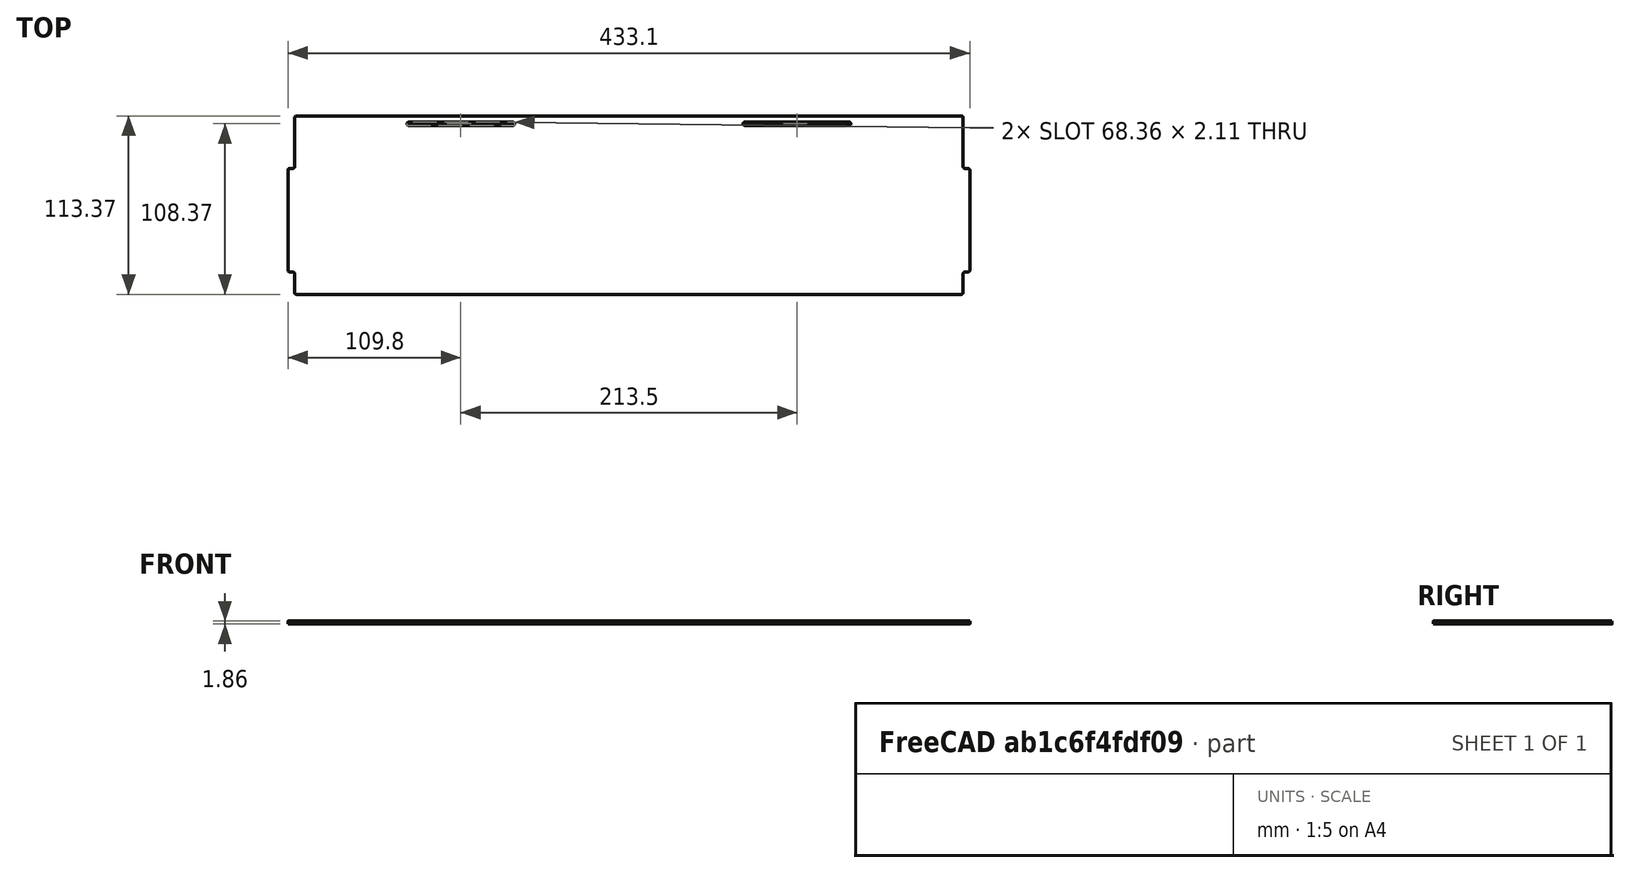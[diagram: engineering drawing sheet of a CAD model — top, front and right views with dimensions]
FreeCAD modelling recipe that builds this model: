
FCSTD DOCUMENT  (FreeCAD 1.0R38641 +468 (Git))
Label: panel_top_and_bottom
License: All rights reserved
LicenseURL: https://en.wikipedia.org/wiki/All_rights_reserved
objects: PartDesign::SubShapeBinder×2, Sketcher::SketchObject×1, PartDesign::Pad×1, PartDesign::Body×1
note: 8 computed .brp shape members not serialized (recipe doc carries the construction recipe); baked Part::Feature solids carry a one-line shape summary decoded from their .brp
EXTERNAL_REF file=dimensions.FCStd obj=VarSet
EXTERNAL_REF file=panel_side.FCStd obj=Sketch
EXTERNAL_REF file=panel_side.FCStd obj=Body001
EXTERNAL_REF file=../third_party/tiptop_z_rail.FCStd obj=Body

FEATURE [PartDesign::SubShapeBinder] Binder  label="SidePanelBinder"
  BindCopyOnChange = 0
  BindMode = 0
  ClaimChildren = false
  Context = -> Body [Binder.]
  Fuse = false
  MakeFace = true
  OffsetFill = false
  OffsetIntersection = false
  OffsetJoinType = 0
  OffsetOpenResult = false
  PartialLoad = false
  Refine = true
  Relative = true
  Support = -> [<external panel_side.FCStd>#Body001]
  _Version = 2
FEATURE [PartDesign::SubShapeBinder] Binder001  label="RailBinder"
  BindCopyOnChange = 0
  BindMode = 0
  ClaimChildren = false
  Context = -> Body [Binder001.]
  Fuse = false
  MakeFace = true
  OffsetFill = false
  OffsetIntersection = false
  OffsetJoinType = 0
  OffsetOpenResult = false
  PartialLoad = false
  Refine = true
  Relative = true
  Support = -> [<external ../third_party/tiptop_z_rail.FCStd>#Body]
  _Version = 2
FEATURE [Sketcher::SketchObject] Sketch
  ArcFitTolerance = 1e-06
  AttachmentOffset = pos=(0,0,0.127) rot=(0,0,1;0rad)
  AttachmentSupport = -> [Binder,Binder001]
  ExternalGeometry = -> [Binder,Binder001]
  FullyConstrained = true
  MakeInternals = false
  MapMode = 5
  Placement = pos=(0,1.3e-15,4.0729) rot=(0,0,1;0rad)
  expr: .AttachmentOffset.Base.z = dimensions#VarSet.EnclosureFinishThickness
  expr: Constraints[102] = dimensions#VarSet.EnclosureFinishThickness
  expr: Constraints[27] = 2 * <<dimensions>>#VarSet.EnclosureFinishThickness
  expr: Constraints[78] = <<dimensions>>#VarSet.EnclosureTotalThickness + 2 * <<dimensions>>#VarSet.EnclosureFinishThickness
  expr: Constraints[87] = <<dimensions>>#VarSet.EnclosureCornerRadius
  expr: Constraints[89] = panel_side#<<Sketch>>.Constraints.EdgeToSlot
  expr: Constraints[90] = panel_side#<<Sketch>>.Constraints.SlotLength
  sketch-geometry (44):
    g0: LineSegment StartX=-3.0542 StartY=96.721 StartZ=0 EndX=-3.0542 EndY=33.379 EndZ=0
    g1: LineSegment StartX=430.054 StartY=33.379 StartZ=0 EndX=430.054 EndY=96.721 EndZ=0
    g2: ArcOfCircle CenterX=-1.8542 CenterY=96.721 CenterZ=0 NormalX=0 NormalY=0 NormalZ=1 AngleXU=0 Radius=1.2 StartAngle=1.5708 EndAngle=3.14159
    g3: ArcOfCircle CenterX=-1.8542 CenterY=33.379 CenterZ=0 NormalX=0 NormalY=0 NormalZ=1 AngleXU=0 Radius=1.2 StartAngle=3.14159 EndAngle=4.71239
    g4: ArcOfCircle CenterX=428.854 CenterY=33.379 CenterZ=0 NormalX=0 NormalY=0 NormalZ=1 AngleXU=0 Radius=1.2 StartAngle=4.71239 EndAngle=6.28319
    g5: ArcOfCircle CenterX=428.854 CenterY=96.721 CenterZ=0 NormalX=0 NormalY=0 NormalZ=1 AngleXU=0 Radius=1.2 StartAngle=-4.4e-15 EndAngle=1.5708
    g6: LineSegment StartX=2.4 StartY=17.927 StartZ=0 EndX=424.6 EndY=17.927 EndZ=0
    g7: LineSegment StartX=424.6 StartY=131.3 StartZ=0 EndX=2.4 EndY=131.3 EndZ=0
    g8: ArcOfCircle CenterX=2.4 CenterY=130.1 CenterZ=0 NormalX=0 NormalY=0 NormalZ=1 AngleXU=0 Radius=1.2 StartAngle=1.5708 EndAngle=3.14159
    g9: ArcOfCircle CenterX=2.4 CenterY=19.127 CenterZ=0 NormalX=0 NormalY=0 NormalZ=1 AngleXU=0 Radius=1.2 StartAngle=3.14159 EndAngle=4.71239
    g10: ArcOfCircle CenterX=424.6 CenterY=19.127 CenterZ=0 NormalX=0 NormalY=0 NormalZ=1 AngleXU=0 Radius=1.2 StartAngle=4.71239 EndAngle=6.28319
    g11: ArcOfCircle CenterX=424.6 CenterY=130.1 CenterZ=0 NormalX=0 NormalY=0 NormalZ=1 AngleXU=0 Radius=1.2 StartAngle=-2.7e-15 EndAngle=1.5708
    g12: LineSegment StartX=428.854 StartY=97.921 StartZ=0 EndX=427 EndY=97.921 EndZ=0
    g13: LineSegment StartX=425.8 StartY=99.121 StartZ=0 EndX=425.8 EndY=130.1 EndZ=0
    g14: LineSegment StartX=425.8 StartY=19.127 StartZ=0 EndX=425.8 EndY=30.979 EndZ=0
    g15: LineSegment StartX=427 StartY=32.179 StartZ=0 EndX=428.854 EndY=32.179 EndZ=0
    g16: LineSegment StartX=-1.8542 StartY=32.179 StartZ=0 EndX=9e-16 EndY=32.179 EndZ=0
    g17: LineSegment StartX=1.2 StartY=30.979 StartZ=0 EndX=1.2 EndY=19.127 EndZ=0
    g18: LineSegment StartX=1.2 StartY=130.1 StartZ=0 EndX=1.2 EndY=99.121 EndZ=0
    g19: LineSegment StartX=1e-15 StartY=97.921 StartZ=0 EndX=-1.8542 EndY=97.921 EndZ=0
    g20: LineSegment [constr] StartX=1e-15 StartY=97.921 StartZ=0 EndX=1e-15 EndY=98.175 EndZ=0
    g21: LineSegment [constr] StartX=1e-15 StartY=32.179 StartZ=0 EndX=1e-15 EndY=31.925 EndZ=0
    g22: ArcOfCircle CenterX=1.2e-15 CenterY=99.121 CenterZ=0 NormalX=0 NormalY=0 NormalZ=1 AngleXU=0 Radius=1.2 StartAngle=4.71239 EndAngle=6.28319
    g23: ArcOfCircle CenterX=9e-16 CenterY=30.979 CenterZ=0 NormalX=0 NormalY=0 NormalZ=1 AngleXU=0 Radius=1.2 StartAngle=-9e-16 EndAngle=1.5708
    g24: ArcOfCircle CenterX=427 CenterY=30.979 CenterZ=0 NormalX=0 NormalY=0 NormalZ=1 AngleXU=0 Radius=1.2 StartAngle=1.5708 EndAngle=3.14159
    g25: ArcOfCircle CenterX=427 CenterY=99.121 CenterZ=0 NormalX=0 NormalY=0 NormalZ=1 AngleXU=0 Radius=1.2 StartAngle=3.14159 EndAngle=4.71239
    g26: LineSegment [constr] StartX=427 StartY=97.921 StartZ=0 EndX=427 EndY=32.179 EndZ=0
    g27: LineSegment [constr] StartX=1.2 StartY=30.979 StartZ=0 EndX=425.8 EndY=30.979 EndZ=0
    g28: ArcOfCircle CenterX=73.625 CenterY=126.3 CenterZ=0 NormalX=0 NormalY=0 NormalZ=1 AngleXU=0 Radius=1.0541 StartAngle=1.5708 EndAngle=4.71239
    g29: ArcOfCircle CenterX=139.875 CenterY=126.3 CenterZ=0 NormalX=0 NormalY=0 NormalZ=1 AngleXU=0 Radius=1.0541 StartAngle=4.71239 EndAngle=7.85398
    g30: LineSegment StartX=73.625 StartY=127.354 StartZ=0 EndX=139.875 EndY=127.354 EndZ=0
    g31: LineSegment StartX=73.625 StartY=125.246 StartZ=0 EndX=139.875 EndY=125.246 EndZ=0
    g32: ArcOfCircle CenterX=287.125 CenterY=126.3 CenterZ=0 NormalX=0 NormalY=0 NormalZ=1 AngleXU=0 Radius=1.0541 StartAngle=1.5708 EndAngle=4.71239
    g33: ArcOfCircle CenterX=353.375 CenterY=126.3 CenterZ=0 NormalX=0 NormalY=0 NormalZ=1 AngleXU=0 Radius=1.0541 StartAngle=4.71239 EndAngle=7.85398
    g34: LineSegment StartX=287.125 StartY=127.354 StartZ=0 EndX=353.375 EndY=127.354 EndZ=0
    g35: LineSegment StartX=287.125 StartY=125.246 StartZ=0 EndX=353.375 EndY=125.246 EndZ=0
    g36: LineSegment [constr] StartX=213.5 StartY=131.3 StartZ=0 EndX=213.5 EndY=17.8 EndZ=0
    g37: LineSegment [constr] StartX=73.625 StartY=127.354 StartZ=0 EndX=73.625 EndY=131.3 EndZ=0
    g38: LineSegment [constr] StartX=287.125 StartY=127.354 StartZ=0 EndX=287.125 EndY=131.3 EndZ=0
    g39: LineSegment [constr] StartX=139.875 StartY=126.3 StartZ=0 EndX=213.5 EndY=126.3 EndZ=0
    g40: LineSegment [constr] StartX=213.5 StartY=126.3 StartZ=0 EndX=287.125 EndY=126.3 EndZ=0
    g41: LineSegment [constr] StartX=106.75 StartY=99.121 StartZ=0 EndX=213.5 EndY=99.121 EndZ=0
    g42: LineSegment [constr] StartX=106.75 StartY=125.246 StartZ=0 EndX=106.75 EndY=99.121 EndZ=0
    g43: LineSegment [constr] StartX=0 StartY=131.3 StartZ=0 EndX=2.4 EndY=131.3 EndZ=0
  constraints (109):
    c: Tangent(g0,g2) = -1.5708
    c: Tangent(g0,g3) = -1.5708
    c: Tangent(g1,g4) = -1.5708
    c: Tangent(g1,g5) = -1.5708
    c: Vertical(g0)
    c: Vertical(g1)
    c: Equal(g2,g3)
    c: Equal(g3,g4)
    c: Equal(g4,g5)
    c: Tangent(g6,g9) = -1.5708
    c: Tangent(g6,g10) = -1.5708
    c: Tangent(g7,g11) = -1.5708
    c: Tangent(g7,g8) = -1.5708
    c: Horizontal(g6)
    c: Horizontal(g7)
    c: Equal(g8,g9)
    c: Equal(g9,g10)
    c: Equal(g10,g11)
    c: Horizontal(g12)
    c: Vertical(g13)
    c: Vertical(g14)
    c: Horizontal(g15)
    c: Horizontal(g16)
    c: Vertical(g17)
    c: Vertical(g18)
    c: Horizontal(g19)
    c: Equal(g21,g20)
    c: Distance(g20,g20) = 0.254
    c: Tangent(g18,g22) = 1.5708
    c: Tangent(g19,g22) = 1.5708
    c: Tangent(g16,g23) = 1.5708
    c: Tangent(g17,g23) = 1.5708
    c: Tangent(g14,g24) = 1.5708
    c: Tangent(g15,g24) = 1.5708
    c: Tangent(g4,g15) = -1.5708
    c: Tangent(g5,g12) = -1.5708
    c: Tangent(g12,g25) = 1.5708
    c: Tangent(g13,g25) = 1.5708
    c: Tangent(g11,g13) = -1.5708
    c: Tangent(g8,g18) = -1.5708
    c: Tangent(g2,g19) = -1.5708
    c: Tangent(g3,g16) = -1.5708
    c: Tangent(g9,g17) = -1.5708
    c: Tangent(g10,g14) = -1.5708
    c: Equal(g22,g23)
    c: Equal(g23,g24)
    c: Equal(g24,g25)
    c: Equal(g2,g22)
    c: Equal(g22,g8)
    c: Coincident(g26,g12)
    c: Coincident(g26,g15)
    c: Vertical(g26)
    c: Coincident(g27,g17)
    c: Coincident(g27,g14)
    c: Horizontal(g27)
    c: Equal(g12,g19)
    c: Coincident(g16,g21)
    c: Coincident(g19,g20)
    c: Tangent(g28,g30) = 1.5708
    c: Tangent(g28,g31) = -1.5708
    c: Tangent(g29,g30) = 1.5708
    c: Tangent(g29,g31) = -1.5708
    c: Equal(g28,g29)
    c: Horizontal(g30)
    c: Tangent(g32,g34) = 1.5708
    c: Tangent(g32,g35) = -1.5708
    c: Tangent(g33,g34) = 1.5708
    c: Tangent(g33,g35) = -1.5708
    c: Equal(g32,g33)
    c: Horizontal(g34)
    c: Symmetric(g7,g7,g36)
    c: Coincident(g37,g28)
    c: Vertical(g37)
    c: Coincident(g38,g32)
    c: PointOnObject(g38,g7)
    c: Vertical(g38)
    c: Equal(g30,g34)
    c: Equal(g32,g29)
    c: Distance(g28,g28) = 2.1082
    c: Coincident(g39,g29)
    c: PointOnObject(g39,g36)
    c: Horizontal(g39)
    c: Coincident(g40,g39)
    c: Coincident(g40,g32)
    c: PointOnObject(g41,g36)
    c: Symmetric(g31,g31,g42)
    c: Vertical(g42)
    c: Radius(g8) = 1.2
    c: PointOnObject(g37,g7)
    c: Distance(g37,g37) = 3.9459
    c: DistanceX(g30,g30) = 66.25
    c: Symmetric(g22,g41,g41)
    c: Coincident(g42,g41)
    c: Horizontal(g41)
    c: Equal(g1,g0)
    c: Coincident(g43,g7)
    c: Horizontal(g43)
    c: Vertical(g20)
    c: Vertical(g21)
    c: Coincident(g20,g-3)
    c: Coincident(g21,g-3)
    c: PointOnObject(g3,g-4)
    c: Distance(g6,g-5) = 0.127
    c: Coincident(g43,g-6)
    c: Symmetric(g-5,g-5,g36)
    c: Horizontal(g40)
    c: Vertical(g36)
    c: Equal(g39,g40)
    c: DistanceY(g0,g0) = 63.342
FEATURE [PartDesign::Pad] Pad
  Direction = (0,0,1)
  Length = 1.8542
  Length2 = 10
  Placement = pos=(0,1.3e-15,4.0729) rot=(0,0,1;0rad)
  Profile = -> Sketch
  ReferenceAxis = -> Sketch [N_Axis]
  Refine = true
  Suppressed = false
  Type = 0
  expr: Length = <<dimensions>>#VarSet.EnclosureTotalThickness
FEATURE [PartDesign::Body] Body  label="PanelTopAndBottom"
  AllowCompound = false
  Group = -> [Sketch,Pad,Binder,Binder001]
  Origin = -> Origin
  Tip = -> Pad
